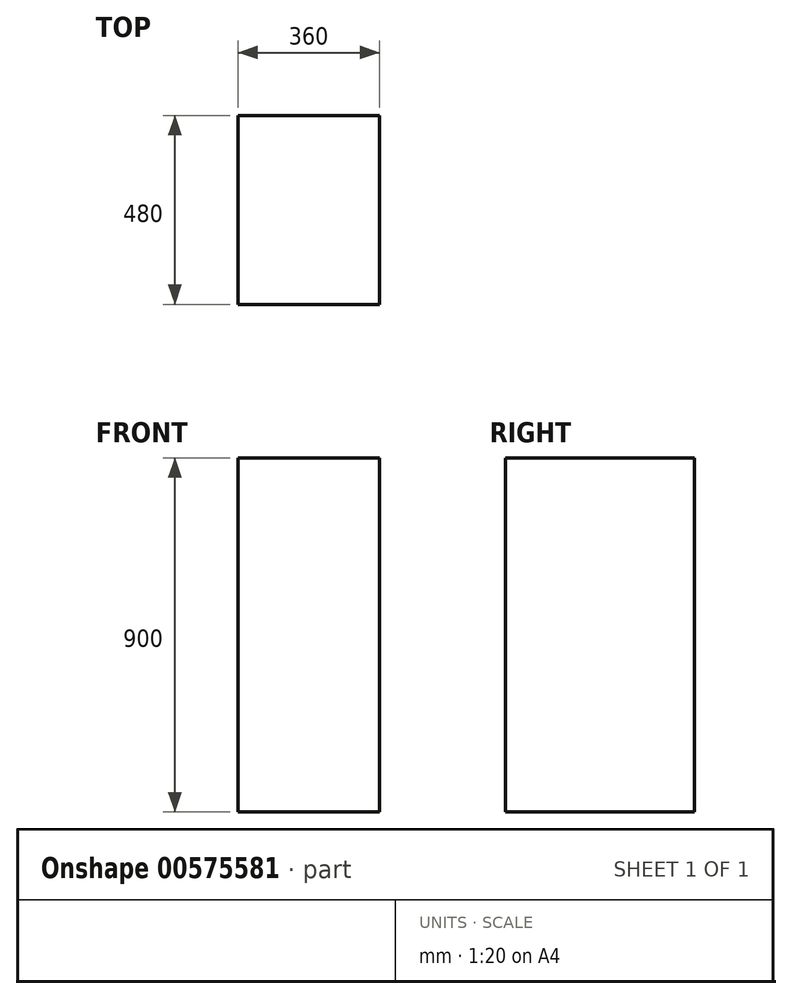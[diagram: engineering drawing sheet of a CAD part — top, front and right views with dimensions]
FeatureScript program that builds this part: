
annotation { "Feature Type Name" : "Feature", "Feature Type Description" : "" }
export const myFeature = defineFeature(function(context is Context, id is Id, definition is map)
    precondition{}
    {
        {
            var Q0;
            Q0=qCreatedBy(makeId("Top.planeOp"),FACE);
            var sketch = newSketch(context, id + "F0", { "sketchPlane" : qUnion([Q0])});
            skLineSegment(sketch, "E0.bottom", {"start": v(0, 0) * mm, "end": v(-360, 0) * mm});
            skLineSegment(sketch, "E0.top", {"start": v(0, 480) * mm, "end": v(-360, 480) * mm});
            skLineSegment(sketch, "E0.left", {"start": v(0, 0) * mm, "end": v(0, 480) * mm});
            skLineSegment(sketch, "E0.right", {"start": v(-360, 0) * mm, "end": v(-360, 480) * mm});
            skSolve(sketch);
        }
        {
            var Q0;
            Q0 = qSketchRegion(id + "F0", true);
            extrude(context, id + "F1", {"entities" : qUnion([Q0]), "depth" : 900 * mm, "offsetDistance" : 25 * mm});
        }
    });
